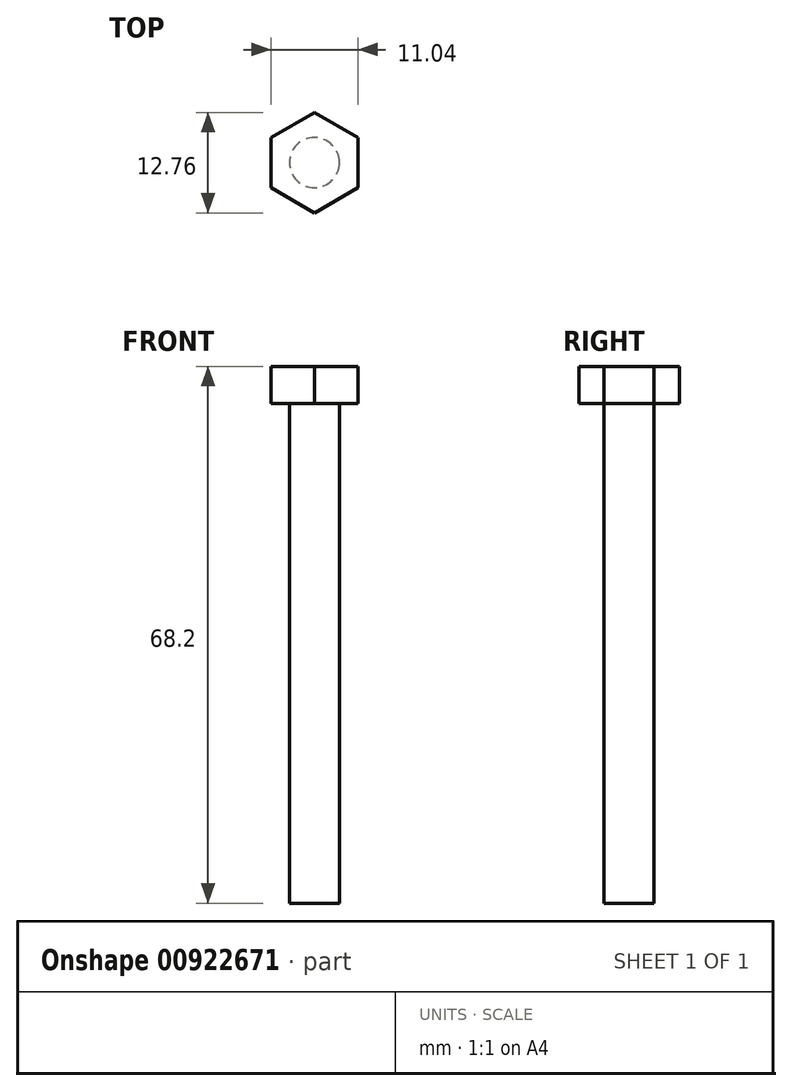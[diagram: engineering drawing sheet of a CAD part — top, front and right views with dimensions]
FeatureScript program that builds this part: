
annotation { "Feature Type Name" : "Feature", "Feature Type Description" : "" }
export const myFeature = defineFeature(function(context is Context, id is Id, definition is map)
    precondition{}
    {
        {
            var Q0;
            Q0=qCreatedBy(makeId("Front.planeOp"),FACE);
            var sketch = newSketch(context, id + "F0", { "sketchPlane" : qUnion([Q0])});
            skLineSegment(sketch, "E0", {"start": v(0, 0) * mm, "end": v(3.18, 0) * mm});
            skLineSegment(sketch, "E1", {"start": v(3.18, 0) * mm, "end": v(3.18, -63.5) * mm});
            skLineSegment(sketch, "E2", {"start": v(3.18, -63.5) * mm, "end": v(0, -63.5) * mm});
            skLineSegment(sketch, "E3", {"start": v(0, -63.5) * mm, "end": v(0, 0) * mm});
            skSolve(sketch);
        }
        {
            var Q0;
            Q0=makeQuery(id+"F0.imprint","IMPRINT",FACE,{"disambiguationData":[TD([[makeQuery(id+"F0.imprint","IMPRINT",EDGE,{"derivedFrom":sQuery(id+"F0.wireOp",EDGE,"E0")}),-1.0]])]});
            var Q1;
            Q1=sQuery(id+"F0.wireOp",EDGE,"E3");
            revolve(context, id + "F1", {"surfaceOperationType" : NewSurfaceOperationType.NEW, "entities" : qUnion([Q0]), "axis" : qUnion([Q1]), "revolveType" : RevolveType.FULL});
        }
        {
            var Q0;
            Q0=makeQuery(id+"F1.opRevolve","SWEPT_FACE",FACE,{"disambiguationData":[OSD([sQuery(id+"F0.wireOp",EDGE,"E0")])]});
            var sketch = newSketch(context, id + "F2", { "sketchPlane" : qUnion([Q0])});
            skCircle(sketch, "E4.cCircle", {"center": v(0, 0) * mm, "radius": 5.52 * mm, "construction": true});
            skLineSegment(sketch, "E4.0", {"start": v(5.52, 3.19) * mm, "end": v(5.52, -3.19) * mm});
            skLineSegment(sketch, "E4.1", {"start": v(5.52, -3.19) * mm, "end": v(0, -6.38) * mm});
            skLineSegment(sketch, "E4.2", {"start": v(0, -6.38) * mm, "end": v(-5.52, -3.19) * mm});
            skLineSegment(sketch, "E4.3", {"start": v(-5.52, -3.19) * mm, "end": v(-5.52, 3.19) * mm});
            skLineSegment(sketch, "E4.4", {"start": v(-5.52, 3.19) * mm, "end": v(0, 6.38) * mm});
            skLineSegment(sketch, "E4.5", {"start": v(0, 6.38) * mm, "end": v(5.52, 3.19) * mm});
            skPoint(sketch, "E4.0.midPoint", {"position": v(5.52, 0) * mm});
            skSolve(sketch);
        }
        {
            var Q0;
            Q0 = qSketchRegion(id + "F2", true);
            extrude(context, id + "F3", {"entities" : qUnion([Q0]), "operationType" : NewBodyOperationType.ADD, "depth" : 4.7 * mm, "offsetDistance" : 25.4 * mm});
        }
    });
